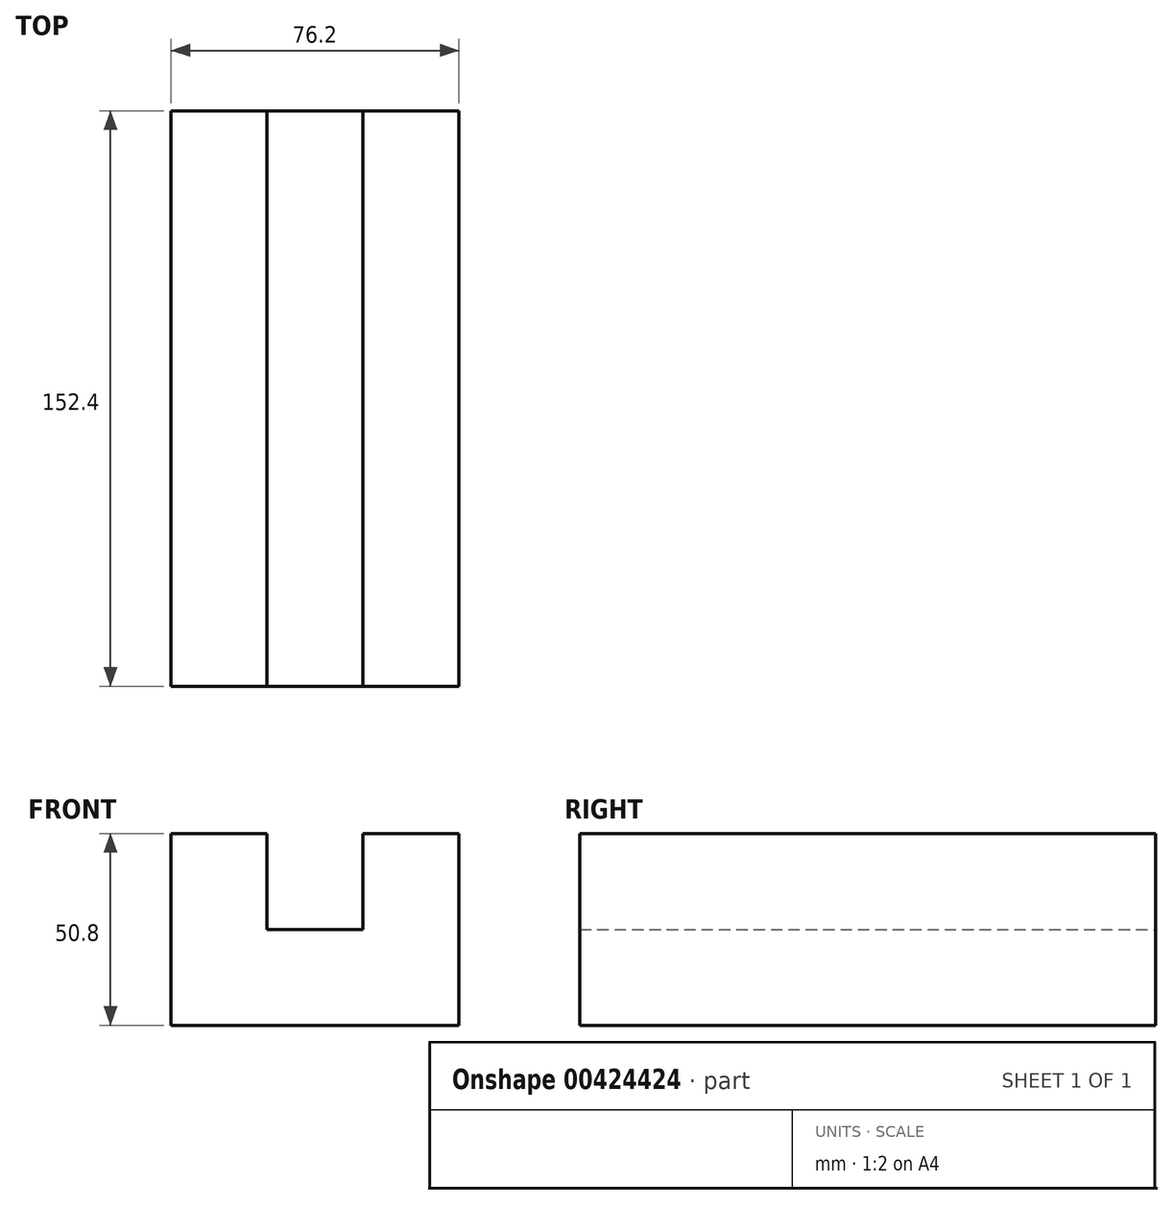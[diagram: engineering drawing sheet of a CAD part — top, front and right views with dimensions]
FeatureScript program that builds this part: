
annotation { "Feature Type Name" : "Feature", "Feature Type Description" : "" }
export const myFeature = defineFeature(function(context is Context, id is Id, definition is map)
    precondition{}
    {
        {
            var Q0;
            Q0=qCreatedBy(makeId("Front.planeOp"),FACE);
            var sketch = newSketch(context, id + "F0", { "sketchPlane" : qUnion([Q0])});
            skLineSegment(sketch, "E0", {"start": v(0, 0) * mm, "end": v(0, 50.8) * mm});
            skLineSegment(sketch, "E1", {"start": v(0, 50.8) * mm, "end": v(25.4, 50.8) * mm});
            skLineSegment(sketch, "E2", {"start": v(25.4, 50.8) * mm, "end": v(25.4, 25.4) * mm});
            skLineSegment(sketch, "E3", {"start": v(25.4, 25.4) * mm, "end": v(50.8, 25.4) * mm});
            skLineSegment(sketch, "E4", {"start": v(50.8, 25.4) * mm, "end": v(50.8, 50.8) * mm});
            skLineSegment(sketch, "E5", {"start": v(50.8, 50.8) * mm, "end": v(76.2, 50.8) * mm});
            skLineSegment(sketch, "E6", {"start": v(76.2, 50.8) * mm, "end": v(76.2, 0) * mm});
            skLineSegment(sketch, "E7", {"start": v(76.2, 0) * mm, "end": v(0, 0) * mm});
            skSolve(sketch);
        }
        {
            var Q0;
            Q0 = qSketchRegion(id + "F0", true);
            extrude(context, id + "F1", {"entities" : qUnion([Q0]), "depth" : 152.4 * mm});
        }
    });
